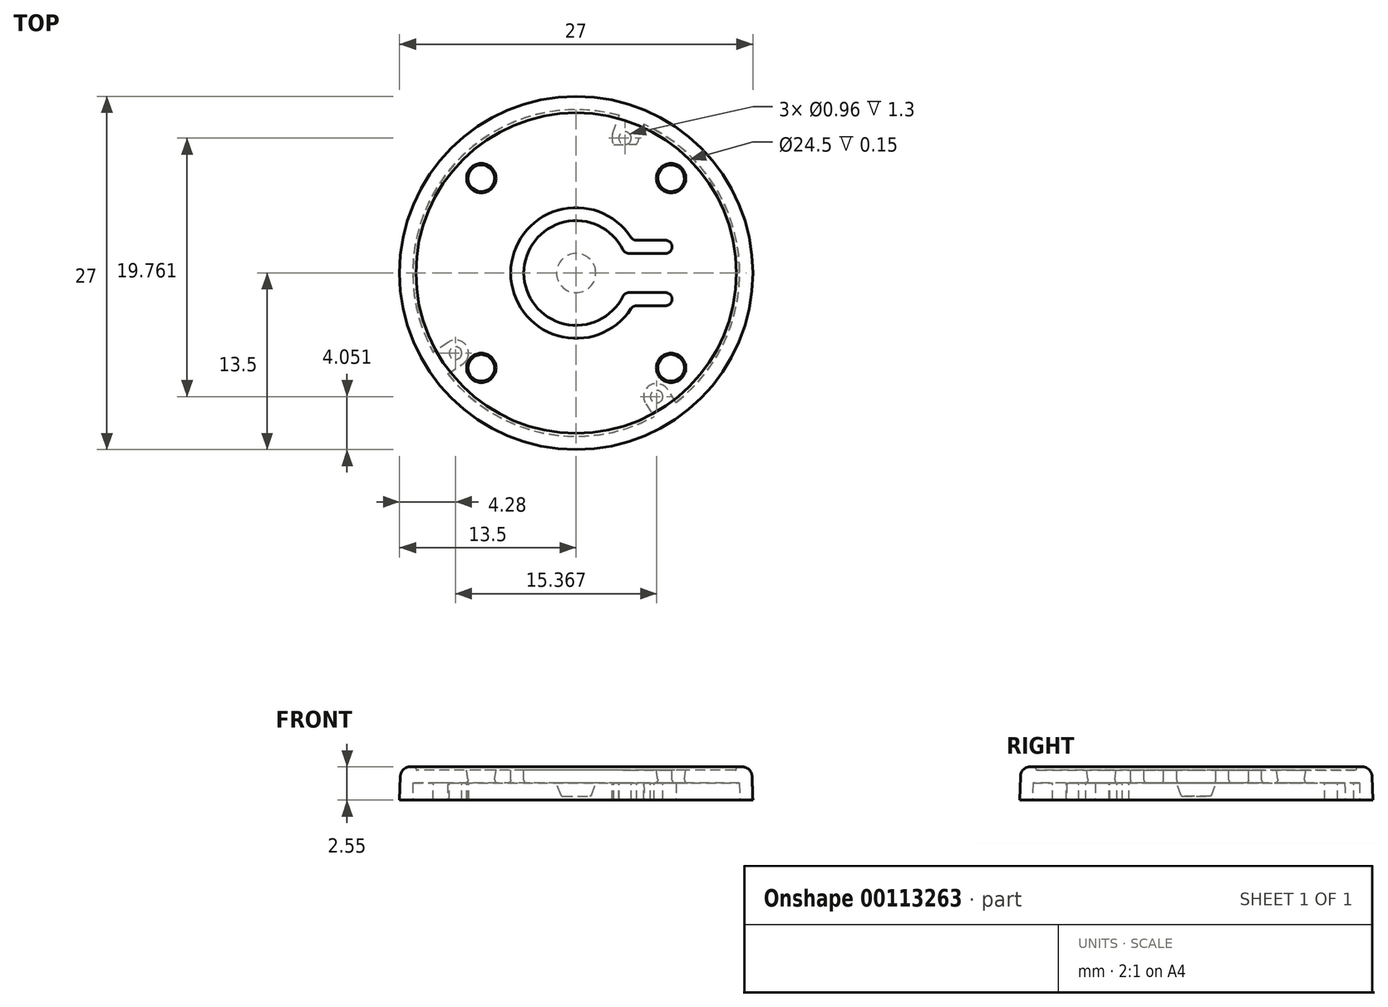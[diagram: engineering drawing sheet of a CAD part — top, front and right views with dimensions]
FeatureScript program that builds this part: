
annotation { "Feature Type Name" : "Feature", "Feature Type Description" : "" }
export const myFeature = defineFeature(function(context is Context, id is Id, definition is map)
    precondition{}
    {
        {
            var Q0;
            Q0=qCreatedBy(makeId("Top.planeOp"),FACE);
            var sketch = newSketch(context, id + "F0", { "sketchPlane" : qUnion([Q0])});
            skCircle(sketch, "E0", {"center": v(0, 0) * mm, "radius": 12.5 * mm});
            skCircle(sketch, "E1.0", {"center": v(0, 0) * mm, "radius": 13.5 * mm});
            skSolve(sketch);
        }
        {
            var Q0;
            Q0=qSketchRegion(id+"F0",true);
            var Q1;
            Q1=makeQuery(id+"F0.imprint","IMPRINT",FACE,{"disambiguationData":[TD([[makeQuery(id+"F0.imprint","IMPRINT",EDGE,{"derivedFrom":sQuery(id+"F0.wireOp",EDGE,"E0")}),1.0]])]});
            extrude(context, id + "F1", {"entities" : qUnion([Q0, Q1]), "depth" : 2.55 * mm, "hasDraft" : true, "draftAngle" : 2 * degree, "draftPullDirection" : true});
        }
        {
            var Q0;
            Q0=makeQuery(id+"F0.imprint","IMPRINT",FACE,{"disambiguationData":[TD([[makeQuery(id+"F0.imprint","IMPRINT",EDGE,{"derivedFrom":sQuery(id+"F0.wireOp",EDGE,"E0")}),1.0]])]});
            extrude(context, id + "F2", {"entities" : qUnion([Q0]), "operationType" : NewBodyOperationType.REMOVE, "depth" : 1.3 * mm, "hasDraft" : true, "draftAngle" : 1 * degree, "draftPullDirection" : true});
        }
        {
            var Q0;
            Q0=makeQuery(id+"F1.opExtrude","CAP_EDGE",EDGE,{"disambiguationData":[OSD([sQuery(id+"F0.wireOp",EDGE,"E1.0")])],"isStart":false});
            fillet(context, id + "F3", {"entities" : qUnion([Q0]), "radius" : .75 * mm, "tangentPropagation" : true, "allowEdgeOverflow" : false});
        }
        {
            var Q0;
            Q0=makeQuery(id+"F1.opExtrude","CAP_FACE",FACE,{"disambiguationData":[OSD([sQuery(id+"F0.wireOp",EDGE,"E1.0")])],"isStart":false});
            var sketch = newSketch(context, id + "F4", { "sketchPlane" : qUnion([Q0])});
            skCircle(sketch, "E2", {"center": v(0, 0) * mm, "radius": 12.25 * mm});
            skSolve(sketch);
        }
        {
            var Q0;
            Q0=qSketchRegion(id+"F4",true);
            extrude(context, id + "F5", {"entities" : qUnion([Q0]), "operationType" : NewBodyOperationType.REMOVE, "oppositeDirection" : true, "depth" : .25 * mm});
        }
        {
            var Q0;
            Q0=makeQuery(id+"F5.boolean.opBoolean","COPY",EDGE,{"derivedFrom":makeQuery(id+"F5.opExtrude","CAP_EDGE",EDGE,{"disambiguationData":[OSD([sQuery(id+"F4.wireOp",EDGE,"E2")])],"isStart":false})});
            var Q1;
            Q1=makeQuery(id+"F5.boolean.opBoolean","COPY",EDGE,{"derivedFrom":makeQuery(id+"F5.opExtrude","CAP_EDGE",EDGE,{"disambiguationData":[OSD([sQuery(id+"F4.wireOp",EDGE,"E2")])],"isStart":true})});
            fillet(context, id + "F6", {"entities" : qUnion([Q0, Q1]), "radius" : .1 * mm, "tangentPropagation" : true, "allowEdgeOverflow" : false});
        }
        {
            var Q0;
            Q0=makeQuery(id+"F5.boolean.opBoolean","COPY",FACE,{"derivedFrom":makeQuery(id+"F5.opExtrude","CAP_FACE",FACE,{"disambiguationData":[OSD([sQuery(id+"F4.wireOp",EDGE,"E2")])],"isStart":false})});
            var sketch = newSketch(context, id + "F7", { "sketchPlane" : qUnion([Q0])});
            skArc(sketch, "E3", {"start": v(3.58, 1.78) * mm, "mid": v(-4, 0) * mm, "end": v(3.58, -1.78) * mm});
            skLineSegment(sketch, "E4", {"start": v(0, 0) * mm, "end": v(11.07, 0) * mm, "construction": true});
            skLineSegment(sketch, "E5", {"start": v(4.03, 1.5) * mm, "end": v(6.83, 1.5) * mm});
            skLineSegment(sketch, "E6", {"start": v(7.33, 2) * mm, "end": v(7.33, 2) * mm});
            skLineSegment(sketch, "E7", {"start": v(6.83, 2.5) * mm, "end": v(4.6, 2.5) * mm});
            skLineSegment(sketch, "E8.0.MirrorCS", {"start": v(4.03, -1.5) * mm, "end": v(6.83, -1.5) * mm});
            skLineSegment(sketch, "E8.1.MirrorCS", {"start": v(6.83, -2.5) * mm, "end": v(4.6, -2.5) * mm});
            skLineSegment(sketch, "E8.2.MirrorCS", {"start": v(7.33, -2) * mm, "end": v(7.33, -2) * mm});
            skArc(sketch, "E9.trimOffspring", {"start": v(4.2, 2.73) * mm, "mid": v(-5, 0) * mm, "end": v(4.2, -2.73) * mm});
            skPoint(sketch, "E10.visualSharp", {"position": v(3.7, 1.5) * mm});
            skArc(sketch, "E10.filletArc", {"start": v(3.58, 1.78) * mm, "mid": v(3.77, 1.58) * mm, "end": v(4.03, 1.5) * mm});
            skPoint(sketch, "E11.visualSharp", {"position": v(4.33, 2.5) * mm});
            skArc(sketch, "E11.filletArc", {"start": v(4.2, 2.73) * mm, "mid": v(4.37, 2.56) * mm, "end": v(4.6, 2.5) * mm});
            skPoint(sketch, "E12.visualSharp", {"position": v(7.33, 2.5) * mm});
            skArc(sketch, "E12.filletArc", {"start": v(7.33, 2) * mm, "mid": v(7.18, 2.35) * mm, "end": v(6.83, 2.5) * mm});
            skPoint(sketch, "E13.visualSharp", {"position": v(7.33, 1.5) * mm});
            skArc(sketch, "E13.filletArc", {"start": v(6.83, 1.5) * mm, "mid": v(7.18, 1.65) * mm, "end": v(7.33, 2) * mm});
            skPoint(sketch, "E14.visualSharp", {"position": v(7.33, -1.5) * mm});
            skArc(sketch, "E14.filletArc", {"start": v(7.33, -2) * mm, "mid": v(7.18, -1.65) * mm, "end": v(6.83, -1.5) * mm});
            skPoint(sketch, "E15.visualSharp", {"position": v(7.33, -2.5) * mm});
            skArc(sketch, "E15.filletArc", {"start": v(6.83, -2.5) * mm, "mid": v(7.18, -2.35) * mm, "end": v(7.33, -2) * mm});
            skPoint(sketch, "E16.visualSharp", {"position": v(4.33, -2.5) * mm});
            skArc(sketch, "E16.filletArc", {"start": v(4.6, -2.5) * mm, "mid": v(4.37, -2.56) * mm, "end": v(4.2, -2.73) * mm});
            skPoint(sketch, "E17.visualSharp", {"position": v(3.7, -1.5) * mm});
            skArc(sketch, "E17.filletArc", {"start": v(4.03, -1.5) * mm, "mid": v(3.77, -1.58) * mm, "end": v(3.58, -1.78) * mm});
            skSolve(sketch);
        }
        {
            var Q0;
            Q0=qSketchRegion(id+"F7",true);
            extrude(context, id + "F8", {"entities" : qUnion([Q0]), "operationType" : NewBodyOperationType.REMOVE, "endBound" : BoundingType.THROUGH_ALL, "oppositeDirection" : true, "depth" : 25 * mm});
        }
        {
            var Q0;
            Q0=makeQuery(id+"F8.boolean.opBoolean","COPY",EDGE,{"derivedFrom":makeQuery(id+"F8.opExtrude","CAP_EDGE",EDGE,{"disambiguationData":[OSD([sQuery(id+"F7.wireOp",EDGE,"E9.trimOffspring")])],"isStart":true})});
            var Q1;
            Q1=makeQuery(id+"F8.boolean.opBoolean","INTERSECT",EDGE,{"derivedFrom":[makeQuery(id+"F2.boolean.opBoolean","COPY",FACE,{"derivedFrom":makeQuery(id+"F2.opExtrude","CAP_FACE",FACE,{"disambiguationData":[OSD([sQuery(id+"F0.wireOp",EDGE,"E0")])],"isStart":false})}),makeQuery(id+"F8.opExtrude","SWEPT_FACE",FACE,{"disambiguationData":[OSD([sQuery(id+"F7.wireOp",EDGE,"E9.trimOffspring")])]})]});
            fillet(context, id + "F9", {"entities" : qUnion([Q0, Q1]), "radius" : .25 * mm, "tangentPropagation" : true, "allowEdgeOverflow" : false});
        }
        {
            var Q0;
            Q0=makeQuery(id+"F2.boolean.opBoolean","COPY",FACE,{"derivedFrom":makeQuery(id+"F2.opExtrude","CAP_FACE",FACE,{"disambiguationData":[OSD([sQuery(id+"F0.wireOp",EDGE,"E0")])],"isStart":false})});
            var sketch = newSketch(context, id + "F10", { "sketchPlane" : qUnion([Q0])});
            skCircle(sketch, "E18", {"center": v(0, 0) * mm, "radius": 1.5 * mm});
            skSolve(sketch);
        }
        {
            var Q0;
            Q0=qSketchRegion(id+"F10",true);
            extrude(context, id + "F11", {"entities" : qUnion([Q0]), "operationType" : NewBodyOperationType.ADD, "depth" : 1 * mm, "hasDraft" : true, "draftAngle" : 20 * degree, "draftPullDirection" : true});
        }
        {
            var Q0;
            Q0=makeQuery(id+"F11.opExtrude","CAP_EDGE",EDGE,{"disambiguationData":[OSD([sQuery(id+"F10.wireOp",EDGE,"E18")])],"isStart":false});
            var Q1;
            Q1=makeQuery(id+"F11.opExtrude","CAP_EDGE",EDGE,{"disambiguationData":[OSD([sQuery(id+"F10.wireOp",EDGE,"E18")])],"isStart":true});
            fillet(context, id + "F12", {"entities" : qUnion([Q0, Q1]), "radius" : .15 * mm, "tangentPropagation" : true, "allowEdgeOverflow" : false});
        }
        {
            var Q0;
            Q0=makeQuery(id+"F5.boolean.opBoolean","COPY",FACE,{"derivedFrom":makeQuery(id+"F5.opExtrude","CAP_FACE",FACE,{"disambiguationData":[OSD([sQuery(id+"F4.wireOp",EDGE,"E2")])],"isStart":false})});
            var sketch = newSketch(context, id + "F13", { "sketchPlane" : qUnion([Q0])});
            skPoint(sketch, "E19.center", {"position": v(0, 0) * mm});
            skLineSegment(sketch, "E20", {"start": v(0, 0) * mm, "end": v(0, 14.83) * mm, "construction": true});
            skCircle(sketch, "E21", {"center": v(-7.25, 7.25) * mm, "radius": 1.13 * mm});
            skCircle(sketch, "E22.1.0", {"center": v(-7.25, -7.25) * mm, "radius": 1.13 * mm});
            skCircle(sketch, "E22.2.0", {"center": v(7.25, -7.25) * mm, "radius": 1.13 * mm});
            skCircle(sketch, "E22.3.0", {"center": v(7.25, 7.25) * mm, "radius": 1.13 * mm});
            skSolve(sketch);
        }
        {
            var Q0;
            Q0=qSketchRegion(id+"F13",true);
            extrude(context, id + "F14", {"entities" : qUnion([Q0]), "operationType" : NewBodyOperationType.REMOVE, "endBound" : BoundingType.THROUGH_ALL, "oppositeDirection" : true, "depth" : 25 * mm, "hasDraft" : true, "draftAngle" : 8 * degree, "draftPullDirection" : true});
        }
        {
            var Q0;
            Q0=makeQuery(id+"F14.boolean.opBoolean","COPY",EDGE,{"derivedFrom":makeQuery(id+"F14.opExtrude","CAP_EDGE",EDGE,{"disambiguationData":[OSD([sQuery(id+"F13.wireOp",EDGE,"E21")])],"isStart":true})});
            var Q1;
            Q1=makeQuery(id+"F14.boolean.opBoolean","COPY",EDGE,{"derivedFrom":makeQuery(id+"F14.opExtrude","CAP_EDGE",EDGE,{"disambiguationData":[OSD([sQuery(id+"F13.wireOp",EDGE,"E22.3.0")])],"isStart":true})});
            var Q2;
            Q2=makeQuery(id+"F14.boolean.opBoolean","COPY",EDGE,{"derivedFrom":makeQuery(id+"F14.opExtrude","CAP_EDGE",EDGE,{"disambiguationData":[OSD([sQuery(id+"F13.wireOp",EDGE,"E22.2.0")])],"isStart":true})});
            var Q3;
            Q3=makeQuery(id+"F14.boolean.opBoolean","COPY",EDGE,{"derivedFrom":makeQuery(id+"F14.opExtrude","CAP_EDGE",EDGE,{"disambiguationData":[OSD([sQuery(id+"F13.wireOp",EDGE,"E22.1.0")])],"isStart":true})});
            var Q4;
            Q4=makeQuery(id+"F14.boolean.opBoolean","INTERSECT",EDGE,{"derivedFrom":[makeQuery(id+"F2.boolean.opBoolean","COPY",FACE,{"derivedFrom":makeQuery(id+"F2.opExtrude","CAP_FACE",FACE,{"disambiguationData":[OSD([sQuery(id+"F0.wireOp",EDGE,"E0")])],"isStart":false})}),makeQuery(id+"F14.opExtrude","SWEPT_FACE",FACE,{"disambiguationData":[OSD([sQuery(id+"F13.wireOp",EDGE,"E22.1.0")])]})]});
            var Q5;
            Q5=makeQuery(id+"F14.boolean.opBoolean","INTERSECT",EDGE,{"derivedFrom":[makeQuery(id+"F2.boolean.opBoolean","COPY",FACE,{"derivedFrom":makeQuery(id+"F2.opExtrude","CAP_FACE",FACE,{"disambiguationData":[OSD([sQuery(id+"F0.wireOp",EDGE,"E0")])],"isStart":false})}),makeQuery(id+"F14.opExtrude","SWEPT_FACE",FACE,{"disambiguationData":[OSD([sQuery(id+"F13.wireOp",EDGE,"E21")])]})]});
            var Q6;
            Q6=makeQuery(id+"F14.boolean.opBoolean","INTERSECT",EDGE,{"derivedFrom":[makeQuery(id+"F2.boolean.opBoolean","COPY",FACE,{"derivedFrom":makeQuery(id+"F2.opExtrude","CAP_FACE",FACE,{"disambiguationData":[OSD([sQuery(id+"F0.wireOp",EDGE,"E0")])],"isStart":false})}),makeQuery(id+"F14.opExtrude","SWEPT_FACE",FACE,{"disambiguationData":[OSD([sQuery(id+"F13.wireOp",EDGE,"E22.3.0")])]})]});
            var Q7;
            Q7=makeQuery(id+"F14.boolean.opBoolean","INTERSECT",EDGE,{"derivedFrom":[makeQuery(id+"F2.boolean.opBoolean","COPY",FACE,{"derivedFrom":makeQuery(id+"F2.opExtrude","CAP_FACE",FACE,{"disambiguationData":[OSD([sQuery(id+"F0.wireOp",EDGE,"E0")])],"isStart":false})}),makeQuery(id+"F14.opExtrude","SWEPT_FACE",FACE,{"disambiguationData":[OSD([sQuery(id+"F13.wireOp",EDGE,"E22.2.0")])]})]});
            fillet(context, id + "F15", {"entities" : qUnion([Q0, Q1, Q2, Q3, Q4, Q5, Q6, Q7]), "radius" : .25 * mm, "tangentPropagation" : true, "allowEdgeOverflow" : false});
        }
        {
            var Q0;
            Q0=makeQuery(id+"F2.boolean.opBoolean","COPY",FACE,{"derivedFrom":makeQuery(id+"F2.opExtrude","CAP_FACE",FACE,{"disambiguationData":[OSD([sQuery(id+"F0.wireOp",EDGE,"E0")])],"isStart":false})});
            var sketch = newSketch(context, id + "F16", { "sketchPlane" : qUnion([Q0])});
            skLineSegment(sketch, "E23", {"start": v(0, 0) * mm, "end": v(6.15, 9.45) * mm, "construction": true});
            skLineSegment(sketch, "E24", {"start": v(0, 0) * mm, "end": v(18.94, 0) * mm, "construction": true});
            skCircle(sketch, "E25", {"center": v(6.15, 9.45) * mm, "radius": 1 * mm});
            skLineSegment(sketch, "E26", {"start": v(0, 0) * mm, "end": v(3.73, -10.31) * mm, "construction": true});
            skCircle(sketch, "E27", {"center": v(3.73, -10.31) * mm, "radius": 1 * mm});
            skLineSegment(sketch, "E28", {"start": v(0, 0) * mm, "end": v(-9.22, 6.12) * mm, "construction": true});
            skCircle(sketch, "E29", {"center": v(-9.22, 6.12) * mm, "radius": 1 * mm});
            skLineSegment(sketch, "E30", {"start": v(2.86, -9.83) * mm, "end": v(4.6, -9.83) * mm});
            skCircle(sketch, "E31", {"center": v(3.73, -10.31) * mm, "radius": 0.48 * mm});
            skCircle(sketch, "E32", {"center": v(-9.22, 6.12) * mm, "radius": 0.48 * mm});
            skCircle(sketch, "E33", {"center": v(6.15, 9.45) * mm, "radius": 0.48 * mm});
            skLineSegment(sketch, "E34", {"start": v(-9.77, 5.29) * mm, "end": v(-11.47, 6.42) * mm});
            skLineSegment(sketch, "E35", {"start": v(-11.47, 6.42) * mm, "end": v(-10.36, 8.08) * mm});
            skLineSegment(sketch, "E36", {"start": v(-10.36, 8.08) * mm, "end": v(-8.67, 6.95) * mm});
            skLineSegment(sketch, "E37", {"start": v(2.8, -10.65) * mm, "end": v(3.45, -12.48) * mm});
            skLineSegment(sketch, "E38", {"start": v(3.45, -12.48) * mm, "end": v(5.32, -11.75) * mm});
            skLineSegment(sketch, "E39", {"start": v(5.32, -11.75) * mm, "end": v(4.67, -9.97) * mm});
            skLineSegment(sketch, "E40", {"start": v(5.3, 10) * mm, "end": v(6.23, 11.41) * mm});
            skLineSegment(sketch, "E41", {"start": v(6.23, 11.41) * mm, "end": v(7.9, 10.32) * mm});
            skLineSegment(sketch, "E42", {"start": v(7.9, 10.32) * mm, "end": v(6.98, 8.9) * mm});
            skSolve(sketch);
        }
        {
            var Q0;
            {var subQ3=sQuery(id+"F16.wireOp",EDGE,"E35");Q0=makeQuery(id+"F16.imprint","IMPRINT",FACE,{"disambiguationData":[TD([[makeQuery(id+"F16.imprint","IMPRINT",EDGE,{"derivedFrom":subQ3}),-1.0]])]});}
            var Q1;
            Q1=makeQuery(id+"F16.imprint","IMPRINT",FACE,{"disambiguationData":[TD([[makeQuery(id+"F16.imprint","IMPRINT",EDGE,{"derivedFrom":sQuery(id+"F16.wireOp",EDGE,"E32")}),-1.0]])]});
            var Q2;
            {var subQ0=sQuery(id+"F16.wireOp",EDGE,"E34");var subQ3=sQuery(id+"F16.wireOp",EDGE,"E29");var subQ4=makeQuery(id+"F16.imprint","INTERSECT",VERTEX,{"derivedFrom":[subQ3,subQ0]});Q2=makeQuery(id+"F16.imprint","IMPRINT",FACE,{"disambiguationData":[TD([[makeQuery(id+"F16.imprint","IMPRINT",EDGE,{"disambiguationData":[TD([[subQ4,1.0]])],"derivedFrom":subQ3}),-1.0]])]});}
            var Q3;
            Q3=makeQuery(id+"F16.imprint","IMPRINT",FACE,{"disambiguationData":[TD([[makeQuery(id+"F16.imprint","IMPRINT",EDGE,{"derivedFrom":sQuery(id+"F16.wireOp",EDGE,"E33")}),-1.0]])]});
            var Q4;
            {var subQ3=sQuery(id+"F16.wireOp",EDGE,"E40");var subQ5=sQuery(id+"F16.wireOp",EDGE,"E25");var subQ7=makeQuery(id+"F16.imprint","INTERSECT",VERTEX,{"derivedFrom":[subQ5,subQ3]});Q4=makeQuery(id+"F16.imprint","IMPRINT",FACE,{"disambiguationData":[TD([[makeQuery(id+"F16.imprint","IMPRINT",EDGE,{"disambiguationData":[TD([[subQ7,1.0]])],"derivedFrom":subQ5}),-1.0]])]});}
            var Q5;
            {var subQ3=sQuery(id+"F16.wireOp",EDGE,"E41");Q5=makeQuery(id+"F16.imprint","IMPRINT",FACE,{"disambiguationData":[TD([[makeQuery(id+"F16.imprint","IMPRINT",EDGE,{"derivedFrom":subQ3}),-1.0]])]});}
            var Q6;
            {var subQ5=sQuery(id+"F16.wireOp",EDGE,"E38");Q6=makeQuery(id+"F16.imprint","IMPRINT",FACE,{"disambiguationData":[TD([[makeQuery(id+"F16.imprint","IMPRINT",EDGE,{"derivedFrom":subQ5}),1.0]])]});}
            var Q7;
            {var subQ3=sQuery(id+"F16.wireOp",EDGE,"E27");var subQ5=sQuery(id+"F16.wireOp",EDGE,"E37");var subQ7=makeQuery(id+"F16.imprint","INTERSECT",VERTEX,{"derivedFrom":[subQ3,subQ5]});Q7=makeQuery(id+"F16.imprint","IMPRINT",FACE,{"disambiguationData":[TD([[makeQuery(id+"F16.imprint","IMPRINT",EDGE,{"disambiguationData":[TD([[subQ7,-1.0]])],"derivedFrom":subQ3}),-1.0]])]});}
            var Q8;
            {var subQ2=sQuery(id+"F16.wireOp",EDGE,"E30");Q8=makeQuery(id+"F16.imprint","IMPRINT",FACE,{"disambiguationData":[TD([[makeQuery(id+"F16.imprint","IMPRINT",EDGE,{"derivedFrom":subQ2}),-1.0]])]});}
            extrude(context, id + "F17", {"entities" : qUnion([Q0, Q1, Q2, Q3, Q4, Q5, Q6, Q7, Q8]), "operationType" : NewBodyOperationType.ADD, "depth" : 1.3 * mm});
        }
    });
